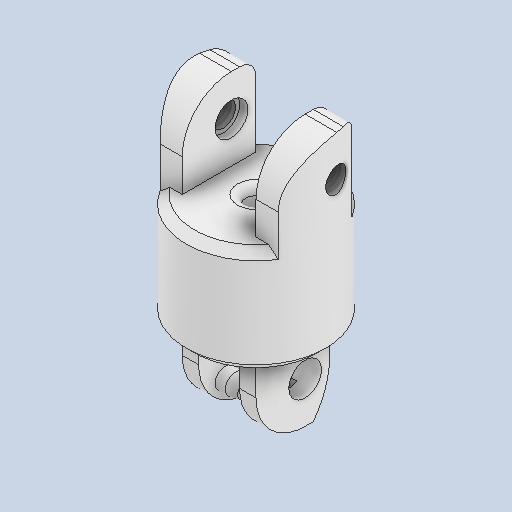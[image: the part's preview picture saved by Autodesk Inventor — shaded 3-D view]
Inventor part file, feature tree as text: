
AUTODESK INVENTOR PART (.ipt)
format: ipt  version: 2022 (Build 260153000, 153)  size: 272,896 bytes
history: native  units: in
note: dims shown in document units (in); Inventor stores cm internally (conversion verified against a paired STEP export)
features: sketch x10, extrude x7, fillet x6, chamfer x4, hole x3, thread x2
ambient origin geometry x8: Origin, YZ Plane, XZ Plane, XY Plane, X Axis, Y Axis, Z Axis, Center Point
bodies: Solid1 (feature_tree)
feature tree (32):
  extrude  "Extrusion1"  Depth=0.3937in
  extrude  "Extrusion2"  Depth=0.0394in TaperAngle=0.0deg
  fillet  "Fillet4"  Radius=0.0394in
  fillet  "Fillet5"  Radius=0.2362in
  fillet  "Fillet6"  Radius=0.3937in
  hole  "Hole1"  [1 undecoded]
  extrude  "Extrusion3"  Depth=0.0492in TaperAngle=0.0deg
  chamfer  "Chamfer1"  Distance=0.0492in Angle=45.0deg
  extrude  "Extrusion4"  Depth=0.0394in TaperAngle=0.0deg
  chamfer  "Chamfer2"  Distance=0.3937in
  extrude  "Extrusion5"  Depth=0.0787in
  fillet  "Fillet8"  Radius=0.1969in
  fillet  "Fillet9"  Radius=0.1969in
  chamfer  "Chamfer3"  Distance=0.0394in Angle=45.0deg
  hole  "Hole2"  [1 undecoded]
  hole  "Hole3"  [1 undecoded]
  chamfer  "Chamfer4"  Distance=0.2362in
  fillet  "Fillet10"  [1 undecoded]
  thread  "Thread1"  [1 undecoded]
  thread  "Thread2"  [1 undecoded]
  sketch  "Sketch1"  dims[d8=0.3937in d9=0.0in d11=0.6693in]
  sketch  "Sketch2"  dims[d12=0.0984in d13=0.0394in d14=0.0in d19=0.0394in d22=0.2362in d23=0.3937in]
  sketch  "Sketch3"  dims[d24=0.1969in]
  sketch  "Sketch4"  dims[d25=0.1575in d26=0.2362in d27=0.1575in d28=0.0787in d29=90.0deg d30=0.3937in d31=0.0in d36=0.0984in d37=0.0in]
  sketch  "Sketch5"  dims[d38=0.0098in d39=0.0492in d40=45.0deg d41=0.0984in d42=0.0in d43=0.0098in d44=0.0492in d45=45.0deg]
  sketch  "Sketch6"  dims[d46=0.4331in d47=0.0in d48=0.0984in d49=0.6693in d51=0.0in d52=0.0394in d55=0.0in d56=0.3937in]
  sketch  "Sketch9"  dims[d63=0.1181in d64=0.2362in d65=0.1575in d66=0.0394in d67=90.0deg d68=0.1575in d69=0.0in d70=0.1969in]
  sketch  "Sketch10"  dims[d71=0.1181in d72=0.2362in d73=0.1575in d74=0.0394in d75=90.0deg d76=0.1575in d77=0.0in d78=0.0394in d79=0.0787in d80=45.0deg d81=0.0394in d82=0.2362in d83=0.0in d84=0.2362in d85=0.0in]
  sketch  "Sketch7"  dims[d57=0.2362in d58=0.0787in]
  sketch  "Sketch8"  dims[d59=0.0394in d60=0.0787in d61=45.0deg d62=0.1969in]
  extrude  "Extrusion6"  [1 undecoded]
  extrude  "Extrusion7"  [1 undecoded]
note: 8 required parameter values undecoded (feature->parameter linkage not recoverable at this tier; creation-order binding heuristic only, values carry confidence <= 0.55)
